# Revit family: DIRIGIBLE 10W_EM10SW.1.15
name_source: partatom
category: Luminarias
units: mm (PartAtom-declared; Revit-internal decimal feet)

## family parameters
Compartido = No
Corte con vacíos al cargar = No
Cota de conector redondo = Diámetro de uso
Origen de luz = Sí
Punto de cálculo de habitación = No
Se basa en plano de trabajo = Sí
Siempre vertical = No
Tipo de pieza = Normal

## types (1)
- EMP_EM10SW.1.15
    Archivo de red fotométrica = EM10SW.1_15°.IES
    Cambio de temperatura de color de luz atenuada = <Ninguno>
    Comentarios de vataje = 100-240V
    Descripción = LUMINARIA TIPO CIRCULAR PARA EMPOTRAR EN PISO CON CUERPO DE ALUMINIO FUNDIDO A PRESION CUBIERTO CON POLVO GRIS OSCURO, CON CUBIERTA DE ACERO INOXIDABLE Y VIDRIO TEMPLADO DE 8MM, HOUSING TIPO ABS DE 179MM DE DIAMETRO Y 220MM DE PROFUNDO. CUENTA CON 9 LED OSRAM CON UNA POTENCIA TOTAL DE 13.2W, A UNA TEMPERATURA EN BLANCO CALIDO CON 756 LUMENES, 112mA EN CORRIENTE DE OPERACIÓN, IP67, IK09, IRC 80, DISPONIBLE PARA ATENUAR EN TRIAC (OPCIONAL), APERTURA EN 15 GRADOS POR PROYECTO, ALIMENTADA A 100-240V
    Elevación por defecto = 0 mm  [stored 0 ft]
    Fabricante = BRILLANT
    Filtro de color = 16777215
    Lámpara = OSRAM
    Modelo = EM10SW.1.15
    Watt per fixture = 13.2
    Ángulo de inclinación = 100.00°

note: [stored X ft] marks values corroborated as IEEE doubles in the binary element streams (Revit-internal decimal feet)

## geometry (parser evidence)
native form markers: Blend x2
no freeform markers — native parametric forms only
